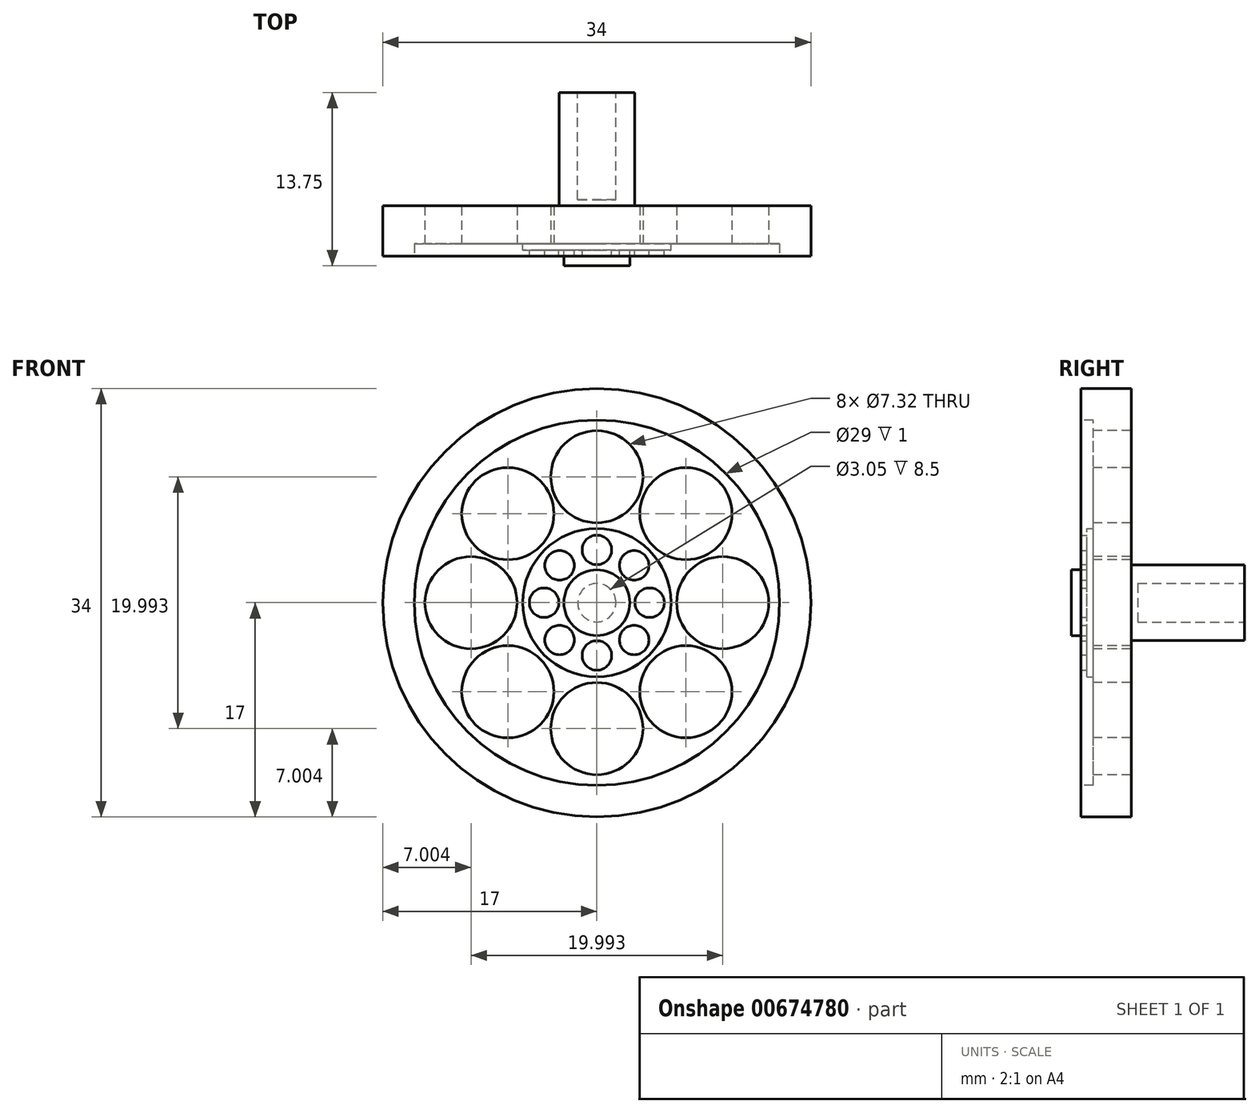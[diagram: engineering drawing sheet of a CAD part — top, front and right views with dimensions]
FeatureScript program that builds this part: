
annotation { "Feature Type Name" : "Feature", "Feature Type Description" : "" }
export const myFeature = defineFeature(function(context is Context, id is Id, definition is map)
    precondition{}
    {
        {
            var Q0;
            Q0=qCreatedBy(makeId("Front.planeOp"),FACE);
            var sketch = newSketch(context, id + "F0", { "sketchPlane" : qUnion([Q0])});
            skCircle(sketch, "E0", {"center": v(0, 0) * mm, "radius": 17 * mm});
            skCircle(sketch, "E1", {"center": v(0, 0) * mm, "radius": 14.5 * mm});
            skSolve(sketch);
        }
        {
            var Q0;
            Q0=makeQuery(id+"F0.imprint","IMPRINT",FACE,{"disambiguationData":[TD([[makeQuery(id+"F0.imprint","IMPRINT",EDGE,{"derivedFrom":sQuery(id+"F0.wireOp",EDGE,"E1")}),1.0]])]});
            var Q1;
            Q1=makeQuery(id+"F0.imprint","IMPRINT",FACE,{"disambiguationData":[TD([[makeQuery(id+"F0.imprint","IMPRINT",EDGE,{"derivedFrom":sQuery(id+"F0.wireOp",EDGE,"E0")}),1.0]])]});
            extrude(context, id + "F1", {"entities" : qUnion([Q0, Q1]), "depth" : 4 * mm, "offsetDistance" : 25 * mm});
        }
        {
            var Q0;
            Q0=makeQuery(id+"F1.opExtrude","CAP_FACE",FACE,{"disambiguationData":[OSD([sQuery(id+"F0.wireOp",EDGE,"E0")])],"isStart":false});
            var sketch = newSketch(context, id + "F2", { "sketchPlane" : qUnion([Q0])});
            skCircle(sketch, "E2", {"center": v(0, 0) * mm, "radius": 14.5 * mm});
            skSolve(sketch);
        }
        {
            var Q0;
            Q0=makeQuery(id+"F2.imprint","IMPRINT",FACE,{"disambiguationData":[TD([[makeQuery(id+"F2.imprint","IMPRINT",EDGE,{"derivedFrom":sQuery(id+"F2.wireOp",EDGE,"E2")}),1.0]])]});
            extrude(context, id + "F3", {"entities" : qUnion([Q0]), "operationType" : NewBodyOperationType.REMOVE, "oppositeDirection" : true, "depth" : 1 * mm, "offsetDistance" : 25 * mm});
        }
        {
            var Q0;
            Q0=makeQuery(id+"F3.boolean.opBoolean","COPY",FACE,{"derivedFrom":makeQuery(id+"F3.opExtrude","CAP_FACE",FACE,{"disambiguationData":[OSD([sQuery(id+"F2.wireOp",EDGE,"E2")])],"isStart":false})});
            var sketch = newSketch(context, id + "F4", { "sketchPlane" : qUnion([Q0])});
            skCircle(sketch, "E3", {"center": v(0, 0) * mm, "radius": 5.5 * mm});
            skCircle(sketch, "E4", {"center": v(0, 10) * mm, "radius": 3.66 * mm});
            skCircle(sketch, "E5.1.0", {"center": v(-7.07, 7.07) * mm, "radius": 3.66 * mm});
            skCircle(sketch, "E5.2.0", {"center": v(-10, 0) * mm, "radius": 3.66 * mm});
            skCircle(sketch, "E5.3.0", {"center": v(-7.07, -7.07) * mm, "radius": 3.66 * mm});
            skCircle(sketch, "E5.4.0", {"center": v(0, -10) * mm, "radius": 3.66 * mm});
            skCircle(sketch, "E5.5.0", {"center": v(7.07, -7.07) * mm, "radius": 3.66 * mm});
            skCircle(sketch, "E5.6.0", {"center": v(10, 0) * mm, "radius": 3.66 * mm});
            skCircle(sketch, "E5.7.0", {"center": v(7.07, 7.07) * mm, "radius": 3.66 * mm});
            skSolve(sketch);
        }
        {
            var Q0;
            Q0=makeQuery(id+"F4.imprint","IMPRINT",FACE,{"disambiguationData":[TD([[makeQuery(id+"F4.imprint","IMPRINT",EDGE,{"derivedFrom":sQuery(id+"F4.wireOp",EDGE,"E5.1.0")}),1.0]])]});
            var Q1;
            Q1=makeQuery(id+"F4.imprint","IMPRINT",FACE,{"disambiguationData":[TD([[makeQuery(id+"F4.imprint","IMPRINT",EDGE,{"derivedFrom":sQuery(id+"F4.wireOp",EDGE,"E5.2.0")}),1.0]])]});
            var Q2;
            Q2=makeQuery(id+"F4.imprint","IMPRINT",FACE,{"disambiguationData":[TD([[makeQuery(id+"F4.imprint","IMPRINT",EDGE,{"derivedFrom":sQuery(id+"F4.wireOp",EDGE,"E4")}),1.0]])]});
            var Q3;
            Q3=makeQuery(id+"F4.imprint","IMPRINT",FACE,{"disambiguationData":[TD([[makeQuery(id+"F4.imprint","IMPRINT",EDGE,{"derivedFrom":sQuery(id+"F4.wireOp",EDGE,"E5.7.0")}),1.0]])]});
            var Q4;
            Q4=makeQuery(id+"F4.imprint","IMPRINT",FACE,{"disambiguationData":[TD([[makeQuery(id+"F4.imprint","IMPRINT",EDGE,{"derivedFrom":sQuery(id+"F4.wireOp",EDGE,"E5.6.0")}),1.0]])]});
            var Q5;
            Q5=makeQuery(id+"F4.imprint","IMPRINT",FACE,{"disambiguationData":[TD([[makeQuery(id+"F4.imprint","IMPRINT",EDGE,{"derivedFrom":sQuery(id+"F4.wireOp",EDGE,"E5.5.0")}),1.0]])]});
            var Q6;
            Q6=makeQuery(id+"F4.imprint","IMPRINT",FACE,{"disambiguationData":[TD([[makeQuery(id+"F4.imprint","IMPRINT",EDGE,{"derivedFrom":sQuery(id+"F4.wireOp",EDGE,"E5.4.0")}),1.0]])]});
            var Q7;
            Q7=makeQuery(id+"F4.imprint","IMPRINT",FACE,{"disambiguationData":[TD([[makeQuery(id+"F4.imprint","IMPRINT",EDGE,{"derivedFrom":sQuery(id+"F4.wireOp",EDGE,"E5.3.0")}),1.0]])]});
            extrude(context, id + "F5", {"entities" : qUnion([Q0, Q1, Q2, Q3, Q4, Q5, Q6, Q7]), "operationType" : NewBodyOperationType.REMOVE, "oppositeDirection" : true, "depth" : 25 * mm, "offsetDistance" : 25 * mm});
        }
        {
            var Q0;
            Q0=makeQuery(id+"F3.boolean.opBoolean","COPY",FACE,{"derivedFrom":makeQuery(id+"F3.opExtrude","CAP_FACE",FACE,{"disambiguationData":[OSD([sQuery(id+"F2.wireOp",EDGE,"E2")])],"isStart":false})});
            var sketch = newSketch(context, id + "F6", { "sketchPlane" : qUnion([Q0])});
            skCircle(sketch, "E6", {"center": v(0, 0) * mm, "radius": 5.89 * mm});
            skSolve(sketch);
        }
        {
            var Q0;
            Q0=makeQuery(id+"F6.imprint","IMPRINT",FACE,{"disambiguationData":[TD([[makeQuery(id+"F6.imprint","IMPRINT",EDGE,{"derivedFrom":sQuery(id+"F6.wireOp",EDGE,"E6")}),1.0]])]});
            extrude(context, id + "F7", {"entities" : qUnion([Q0]), "operationType" : NewBodyOperationType.ADD, "depth" : .5 * mm, "offsetDistance" : 25 * mm});
        }
        {
            var Q0;
            Q0=makeQuery(id+"F7.opExtrude","CAP_FACE",FACE,{"disambiguationData":[OSD([sQuery(id+"F6.wireOp",EDGE,"E6")])],"isStart":false});
            var sketch = newSketch(context, id + "F8", { "sketchPlane" : qUnion([Q0])});
            skCircle(sketch, "E7", {"center": v(0, 4.19) * mm, "radius": 1.17 * mm});
            skCircle(sketch, "E8.1.0", {"center": v(-2.96, 2.96) * mm, "radius": 1.17 * mm});
            skCircle(sketch, "E8.2.0", {"center": v(-4.19, 0) * mm, "radius": 1.17 * mm});
            skCircle(sketch, "E8.3.0", {"center": v(-2.96, -2.96) * mm, "radius": 1.17 * mm});
            skCircle(sketch, "E8.4.0", {"center": v(0, -4.19) * mm, "radius": 1.17 * mm});
            skCircle(sketch, "E8.5.0", {"center": v(2.96, -2.96) * mm, "radius": 1.17 * mm});
            skCircle(sketch, "E8.6.0", {"center": v(4.19, 0) * mm, "radius": 1.17 * mm});
            skCircle(sketch, "E8.7.0", {"center": v(2.96, 2.96) * mm, "radius": 1.17 * mm});
            skPoint(sketch, "E8.center", {"position": v(0, 0) * mm});
            skSolve(sketch);
        }
        {
            var Q0;
            Q0=makeQuery(id+"F8.imprint","IMPRINT",FACE,{"disambiguationData":[TD([[makeQuery(id+"F8.imprint","IMPRINT",EDGE,{"derivedFrom":sQuery(id+"F8.wireOp",EDGE,"E8.1.0")}),1.0]])]});
            var Q1;
            Q1=makeQuery(id+"F8.imprint","IMPRINT",FACE,{"disambiguationData":[TD([[makeQuery(id+"F8.imprint","IMPRINT",EDGE,{"derivedFrom":sQuery(id+"F8.wireOp",EDGE,"E7")}),1.0]])]});
            var Q2;
            Q2=makeQuery(id+"F8.imprint","IMPRINT",FACE,{"disambiguationData":[TD([[makeQuery(id+"F8.imprint","IMPRINT",EDGE,{"derivedFrom":sQuery(id+"F8.wireOp",EDGE,"E8.7.0")}),1.0]])]});
            var Q3;
            Q3=makeQuery(id+"F8.imprint","IMPRINT",FACE,{"disambiguationData":[TD([[makeQuery(id+"F8.imprint","IMPRINT",EDGE,{"derivedFrom":sQuery(id+"F8.wireOp",EDGE,"E8.6.0")}),1.0]])]});
            var Q4;
            Q4=makeQuery(id+"F8.imprint","IMPRINT",FACE,{"disambiguationData":[TD([[makeQuery(id+"F8.imprint","IMPRINT",EDGE,{"derivedFrom":sQuery(id+"F8.wireOp",EDGE,"E8.5.0")}),1.0]])]});
            var Q5;
            Q5=makeQuery(id+"F8.imprint","IMPRINT",FACE,{"disambiguationData":[TD([[makeQuery(id+"F8.imprint","IMPRINT",EDGE,{"derivedFrom":sQuery(id+"F8.wireOp",EDGE,"E8.4.0")}),1.0]])]});
            var Q6;
            Q6=makeQuery(id+"F8.imprint","IMPRINT",FACE,{"disambiguationData":[TD([[makeQuery(id+"F8.imprint","IMPRINT",EDGE,{"derivedFrom":sQuery(id+"F8.wireOp",EDGE,"E8.3.0")}),1.0]])]});
            var Q7;
            Q7=makeQuery(id+"F8.imprint","IMPRINT",FACE,{"disambiguationData":[TD([[makeQuery(id+"F8.imprint","IMPRINT",EDGE,{"derivedFrom":sQuery(id+"F8.wireOp",EDGE,"E8.2.0")}),1.0]])]});
            extrude(context, id + "F9", {"entities" : qUnion([Q0, Q1, Q2, Q3, Q4, Q5, Q6, Q7]), "operationType" : NewBodyOperationType.ADD, "depth" : .5 * mm, "offsetDistance" : 25 * mm});
        }
        {
            var Q0;
            Q0=makeQuery(id+"F7.opExtrude","CAP_FACE",FACE,{"disambiguationData":[OSD([sQuery(id+"F6.wireOp",EDGE,"E6")])],"isStart":false});
            var sketch = newSketch(context, id + "F10", { "sketchPlane" : qUnion([Q0])});
            skCircle(sketch, "E9", {"center": v(0, 0) * mm, "radius": 2.62 * mm});
            skSolve(sketch);
        }
        {
            var Q0;
            Q0=makeQuery(id+"F10.imprint","IMPRINT",FACE,{"disambiguationData":[TD([[makeQuery(id+"F10.imprint","IMPRINT",EDGE,{"derivedFrom":sQuery(id+"F10.wireOp",EDGE,"E9")}),1.0]])]});
            extrude(context, id + "F11", {"entities" : qUnion([Q0]), "operationType" : NewBodyOperationType.ADD, "depth" : 1.25 * mm, "offsetDistance" : 25 * mm});
        }
        {
            var Q0;
            Q0=makeQuery(id+"F1.opExtrude","CAP_FACE",FACE,{"disambiguationData":[OSD([sQuery(id+"F0.wireOp",EDGE,"E0")])],"isStart":true});
            var sketch = newSketch(context, id + "F12", { "sketchPlane" : qUnion([Q0])});
            skCircle(sketch, "E10", {"center": v(0, 0) * mm, "radius": 3 * mm});
            skSolve(sketch);
        }
        {
            var Q0;
            Q0=makeQuery(id+"F12.imprint","IMPRINT",FACE,{"disambiguationData":[TD([[makeQuery(id+"F12.imprint","IMPRINT",EDGE,{"derivedFrom":sQuery(id+"F12.wireOp",EDGE,"E10")}),1.0]])]});
            extrude(context, id + "F13", {"entities" : qUnion([Q0]), "operationType" : NewBodyOperationType.ADD, "depth" : 9 * mm, "offsetDistance" : 25 * mm});
        }
        {
            var Q0;
            Q0=makeQuery(id+"F13.opExtrude","CAP_FACE",FACE,{"disambiguationData":[OSD([sQuery(id+"F12.wireOp",EDGE,"E10")])],"isStart":false});
            var sketch = newSketch(context, id + "F14", { "sketchPlane" : qUnion([Q0])});
            skCircle(sketch, "E11", {"center": v(0, 0) * mm, "radius": 1.52 * mm});
            skSolve(sketch);
        }
        {
            var Q0;
            Q0=makeQuery(id+"F14.imprint","IMPRINT",FACE,{"disambiguationData":[TD([[makeQuery(id+"F14.imprint","IMPRINT",EDGE,{"derivedFrom":sQuery(id+"F14.wireOp",EDGE,"E11")}),1.0]])]});
            extrude(context, id + "F15", {"entities" : qUnion([Q0]), "operationType" : NewBodyOperationType.REMOVE, "oppositeDirection" : true, "depth" : 8.5 * mm, "offsetDistance" : 25 * mm});
        }
    });
